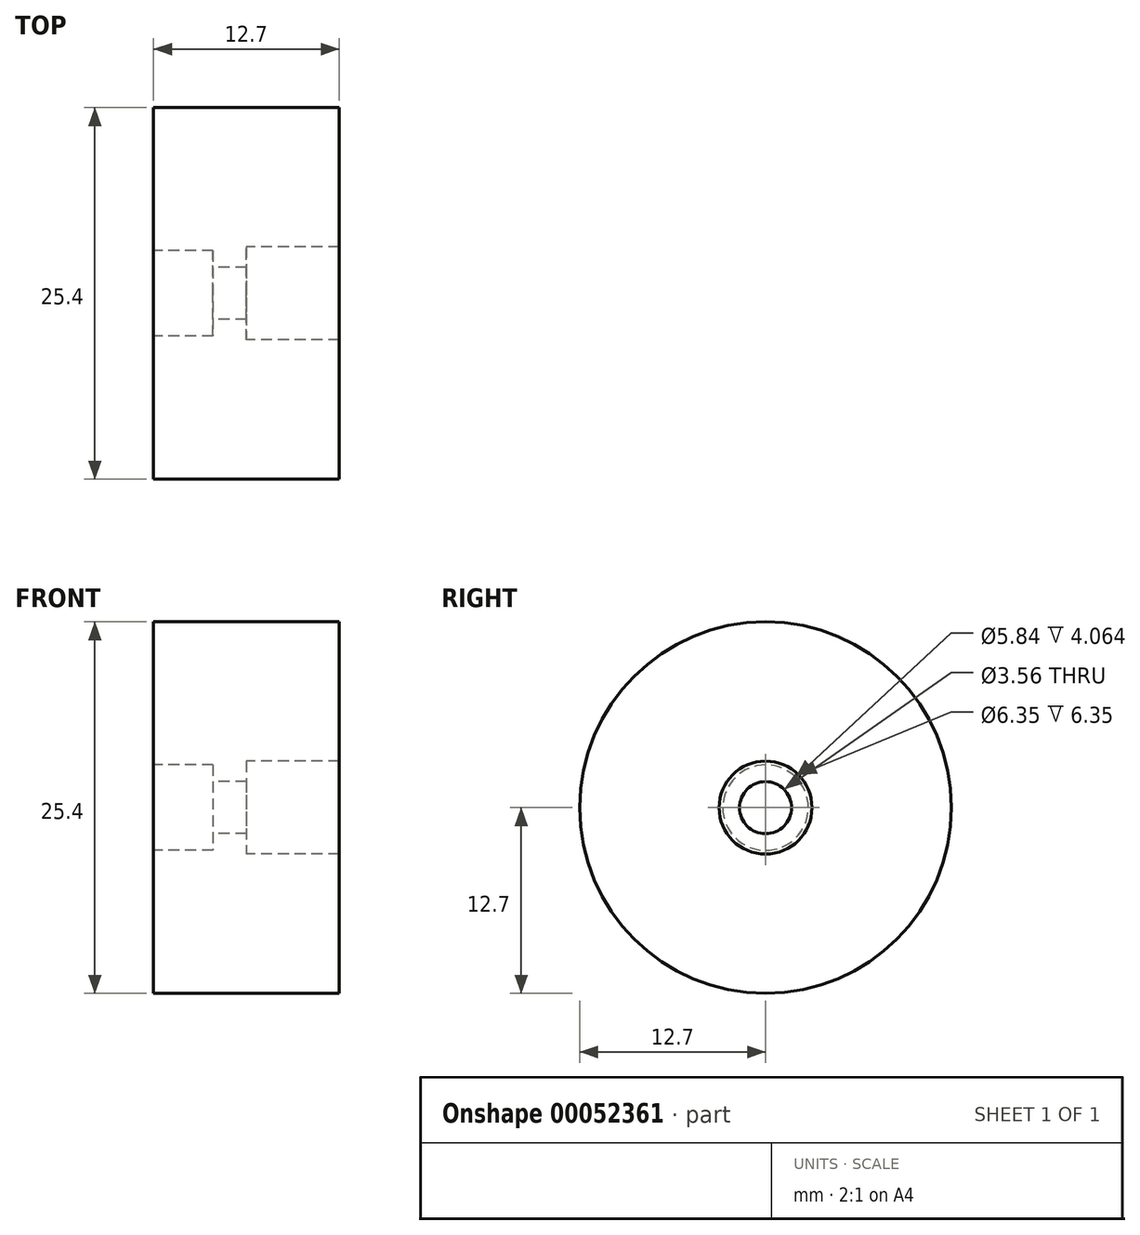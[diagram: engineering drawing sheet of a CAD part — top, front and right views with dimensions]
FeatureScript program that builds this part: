
annotation { "Feature Type Name" : "Feature", "Feature Type Description" : "" }
export const myFeature = defineFeature(function(context is Context, id is Id, definition is map)
    precondition{}
    {
        {
            var Q0;
            Q0=qCreatedBy(makeId("Front.planeOp"),FACE);
            var sketch = newSketch(context, id + "F0", { "sketchPlane" : qUnion([Q0])});
            skLineSegment(sketch, "E0", {"start": v(-44.24, 0) * mm, "end": v(42.95, 0) * mm, "construction": true});
            skLineSegment(sketch, "E1", {"start": v(-6.35, 2.92) * mm, "end": v(-6.35, 12.7) * mm});
            skLineSegment(sketch, "E2", {"start": v(-6.35, 12.7) * mm, "end": v(6.35, 12.7) * mm});
            skLineSegment(sketch, "E3", {"start": v(6.35, 12.7) * mm, "end": v(6.35, 3.17) * mm});
            skLineSegment(sketch, "E4", {"start": v(6.35, 3.18) * mm, "end": v(0, 3.17) * mm});
            skLineSegment(sketch, "E5", {"start": v(0, 3.17) * mm, "end": v(0, 1.78) * mm});
            skLineSegment(sketch, "E6", {"start": v(0, 1.78) * mm, "end": v(-2.29, 1.78) * mm});
            skLineSegment(sketch, "E7", {"start": v(-2.29, 1.78) * mm, "end": v(-2.29, 2.92) * mm});
            skLineSegment(sketch, "E8", {"start": v(-2.29, 2.92) * mm, "end": v(-6.35, 2.92) * mm});
            skPoint(sketch, "E9", {"position": v(0, 12.7) * mm});
            skSolve(sketch);
        }
        {
            var Q0;
            Q0 = qSketchRegion(id + "F0", true);
            var Q1;
            Q1=sQuery(id+"F0.wireOp",EDGE,"E0");
            revolve(context, id + "F1", {"entities" : qUnion([Q0]), "axis" : qUnion([Q1]), "revolveType" : RevolveType.FULL});
        }
    });
